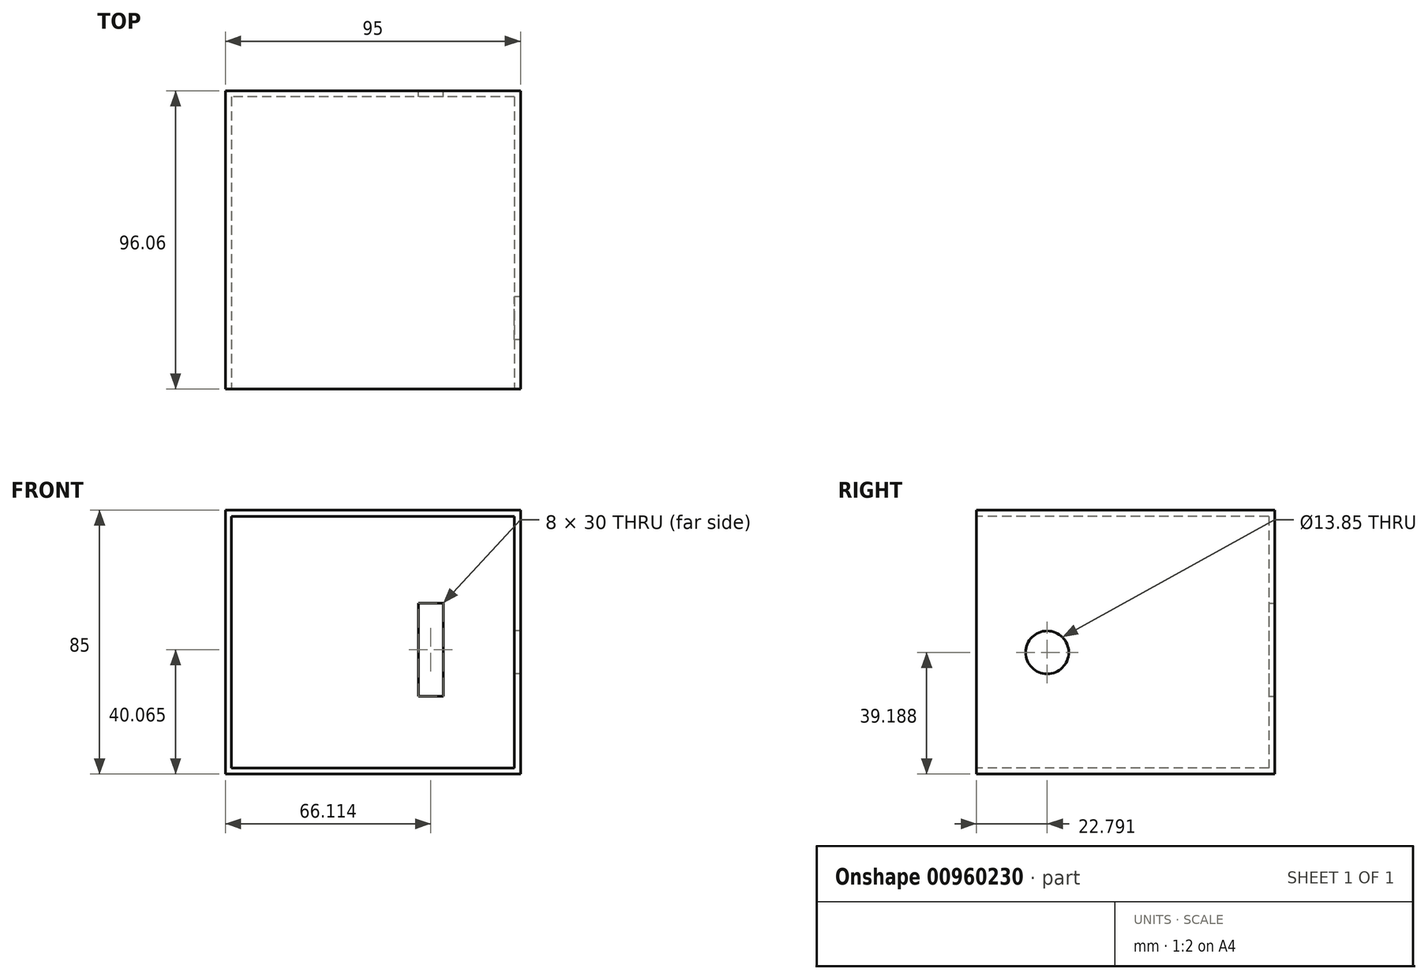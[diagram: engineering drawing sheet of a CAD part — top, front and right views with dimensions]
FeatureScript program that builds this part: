
annotation { "Feature Type Name" : "Feature", "Feature Type Description" : "" }
export const myFeature = defineFeature(function(context is Context, id is Id, definition is map)
    precondition{}
    {
        {
            var Q0;
            Q0=qCreatedBy(makeId("Top.planeOp"),FACE);
            var sketch = newSketch(context, id + "F0", { "sketchPlane" : qUnion([Q0])});
            skLineSegment(sketch, "E0.bottom", {"start": v(0, 0) * mm, "end": v(-95, 0) * mm});
            skLineSegment(sketch, "E0.top", {"start": v(0, -96.06) * mm, "end": v(-95, -96.06) * mm});
            skLineSegment(sketch, "E0.left", {"start": v(0, 0) * mm, "end": v(0, -96.06) * mm});
            skLineSegment(sketch, "E0.right", {"start": v(-95, 0) * mm, "end": v(-95, -96.06) * mm});
            skSolve(sketch);
        }
        {
            var Q0;
            Q0 = qSketchRegion(id + "F0", true);
            extrude(context, id + "F1", {"entities" : qUnion([Q0]), "depth" : 85 * mm, "offsetDistance" : 25 * mm});
        }
        {
            var Q0;
            Q0=makeQuery(id+"F1.opExtrude","SWEPT_FACE",FACE,{"disambiguationData":[OSD([sQuery(id+"F0.wireOp",EDGE,"E0.top")])]});
            shell(context, id + "F2", {"entities" : qUnion([Q0]), "thickness" : 2 * mm});
        }
        {
            var Q0;
            Q0=makeQuery(id+"F1.opExtrude","SWEPT_FACE",FACE,{"disambiguationData":[OSD([sQuery(id+"F0.wireOp",EDGE,"E0.left")])]});
            var sketch = newSketch(context, id + "F3", { "sketchPlane" : qUnion([Q0])});
            skCircle(sketch, "E1", {"center": v(-73.27, 39.19) * mm, "radius": 6.92 * mm});
            skSolve(sketch);
        }
        {
            var Q0;
            Q0 = qSketchRegion(id + "F3", true);
            extrude(context, id + "F4", {"entities" : qUnion([Q0]), "operationType" : NewBodyOperationType.ADD, "oppositeDirection" : true, "depth" : 65.17 * mm, "offsetDistance" : 25 * mm});
        }
        {
            var Q0;
            Q0=makeQuery(id+"F4.opExtrude","CAP_FACE",FACE,{"disambiguationData":[OSD([sQuery(id+"F3.wireOp",EDGE,"E1")])],"isStart":false});
            extrude(context, id + "F5", {"entities" : qUnion([Q0]), "operationType" : NewBodyOperationType.REMOVE, "oppositeDirection" : true, "depth" : 140.46 * mm, "offsetDistance" : 25 * mm});
        }
        {
            var Q0;
            Q0=makeQuery(id+"F1.opExtrude","SWEPT_FACE",FACE,{"disambiguationData":[OSD([sQuery(id+"F0.wireOp",EDGE,"E0.bottom")])]});
            var sketch = newSketch(context, id + "F6", { "sketchPlane" : qUnion([Q0])});
            skLineSegment(sketch, "E2.bottom", {"start": v(32.89, 25.07) * mm, "end": v(24.89, 25.07) * mm});
            skLineSegment(sketch, "E2.top", {"start": v(32.89, 55.07) * mm, "end": v(24.89, 55.07) * mm});
            skLineSegment(sketch, "E2.left", {"start": v(32.89, 25.07) * mm, "end": v(32.89, 55.07) * mm});
            skLineSegment(sketch, "E2.right", {"start": v(24.89, 25.07) * mm, "end": v(24.89, 55.07) * mm});
            skSolve(sketch);
        }
        {
            var Q0;
            Q0 = qSketchRegion(id + "F6", true);
            extrude(context, id + "F7", {"entities" : qUnion([Q0]), "operationType" : NewBodyOperationType.REMOVE, "oppositeDirection" : true, "depth" : 21.4 * mm, "offsetDistance" : 25 * mm});
        }
    });
